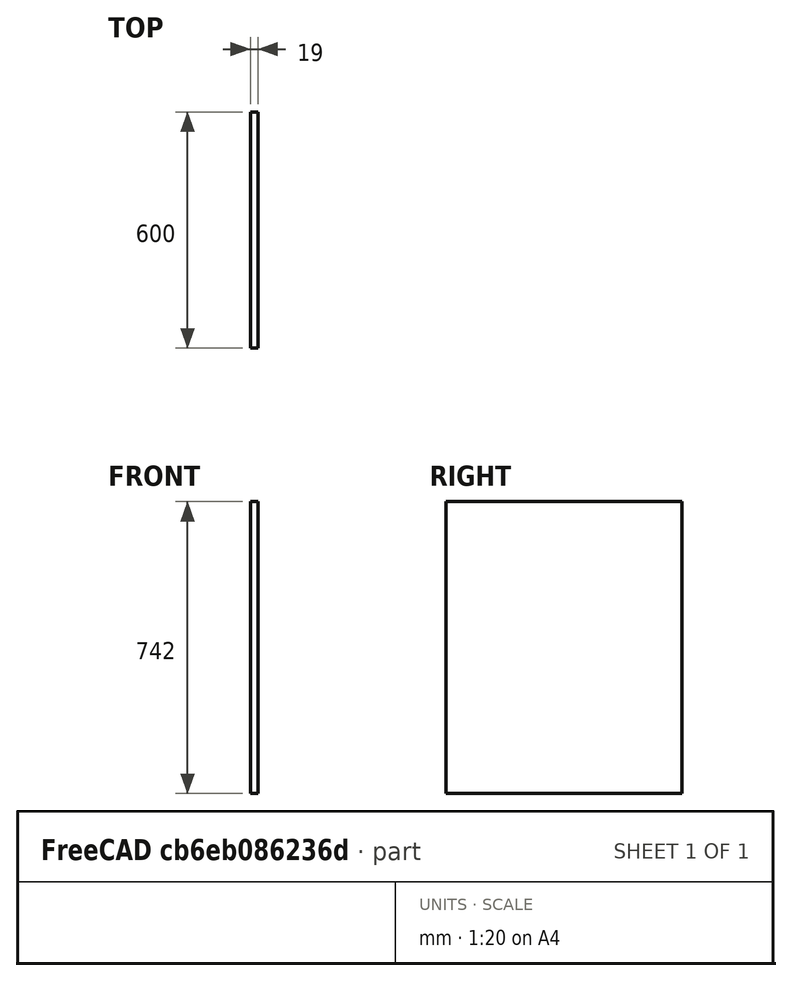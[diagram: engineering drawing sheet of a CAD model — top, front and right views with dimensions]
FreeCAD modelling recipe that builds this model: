
FCSTD DOCUMENT  (FreeCAD 1.0RUnknown)
Label: wardrobe_right_corpus02_jan
License: All rights reserved
LicenseURL: https://en.wikipedia.org/wiki/All_rights_reserved
objects: Sketcher::SketchObject×1, PartDesign::Pad×1, PartDesign::CoordinateSystem×1, PartDesign::Body×1
note: 7 computed .brp shape members not serialized (recipe doc carries the construction recipe); baked Part::Feature solids carry a one-line shape summary decoded from their .brp
EXTERNAL_REF file=../../mastersketch.FCStd obj=Spreadsheet

FEATURE [Sketcher::SketchObject] Sketch002
  ArcFitTolerance = 1e-06
  AttachmentSupport = -> [YZ_Plane004]
  FullyConstrained = true
  MakeInternals = false
  MapMode = 5
  Placement = pos=(0,0,0) rot=(0.57735,0.57735,0.57735;2.0944rad)
  expr: Constraints[10] = mastersketch#Spreadsheet.corpus_depth
  expr: Constraints[11] = mastersketch#Spreadsheet.corpus02_height - 2 * mastersketch#Spreadsheet.corpus_outer_thickness
  sketch-geometry (5):
    g0: LineSegment StartX=-300 StartY=-371 StartZ=0 EndX=300 EndY=-371 EndZ=0
    g1: LineSegment StartX=300 StartY=-371 StartZ=0 EndX=300 EndY=371 EndZ=0
    g2: LineSegment StartX=300 StartY=371 StartZ=0 EndX=-300 EndY=371 EndZ=0
    g3: LineSegment StartX=-300 StartY=371 StartZ=0 EndX=-300 EndY=-371 EndZ=0
    g4: GeomPoint [constr] X=0 Y=0 Z=0
  constraints (12):
    c: Coincident(g0,g1)
    c: Coincident(g1,g2)
    c: Coincident(g2,g3)
    c: Coincident(g3,g0)
    c: Horizontal(g0)
    c: Horizontal(g2)
    c: Vertical(g1)
    c: Vertical(g3)
    c: Symmetric(g2,g0,g4)
    c: Coincident(g4,g-1)
    c: DistanceX(g0,g0) = 600
    c: DistanceY(g3,g3) = 742
FEATURE [PartDesign::Pad] Pad002
  Direction = (1,0,0)
  Length = 19
  Length2 = 10
  Placement = pos=(0,0,0) rot=(1,1,1;2.0944rad)
  Profile = -> Sketch002
  ReferenceAxis = -> Sketch002 [N_Axis]
  Refine = true
  Suppressed = false
  Type = 0
  expr: Length = mastersketch#Spreadsheet.corpus_outer_thickness
FEATURE [PartDesign::CoordinateSystem] LCS_1
  AttacherType = Attacher::AttachEngine3D
  AttachmentSupport = -> [Pad002]
  MapMode = 45
  Placement = pos=(19,-1.82e-14,-371) rot=(0,0.707107,0.707107;3.14159rad)
FEATURE [PartDesign::Body] Body002  label="wardrobe_right_corpus02_jan"
  AllowCompound = false
  Group = -> [Sketch002,Pad002,LCS_1]
  Origin = -> Origin004
  Tip = -> Pad002
